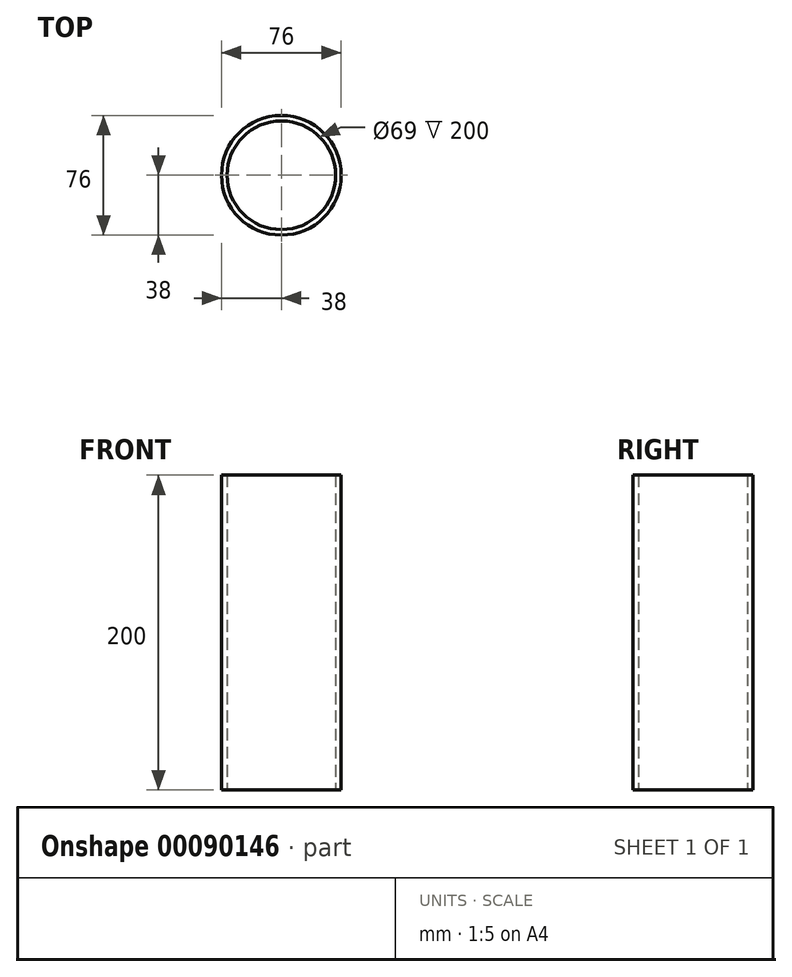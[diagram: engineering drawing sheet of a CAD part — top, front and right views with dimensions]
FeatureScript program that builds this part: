
annotation { "Feature Type Name" : "Feature", "Feature Type Description" : "" }
export const myFeature = defineFeature(function(context is Context, id is Id, definition is map)
    precondition{}
    {
        {
            var Q0;
            Q0=qCreatedBy(makeId("Top.planeOp"),FACE);
            var sketch = newSketch(context, id + "F0", { "sketchPlane" : qUnion([Q0])});
            skCircle(sketch, "E0", {"center": v(0, 0) * mm, "radius": 34.5 * mm});
            skCircle(sketch, "E1", {"center": v(0, 0) * mm, "radius": 38 * mm});
            skSolve(sketch);
        }
        {
            var Q0;
            Q0=makeQuery(id+"F0.imprint","IMPRINT",FACE,{"disambiguationData":[TD([[makeQuery(id+"F0.imprint","IMPRINT",EDGE,{"derivedFrom":sQuery(id+"F0.wireOp",EDGE,"E0")}),-1.0]])]});
            extrude(context, id + "F1", {"entities" : qUnion([Q0]), "depth" : 200 * mm});
        }
    });
